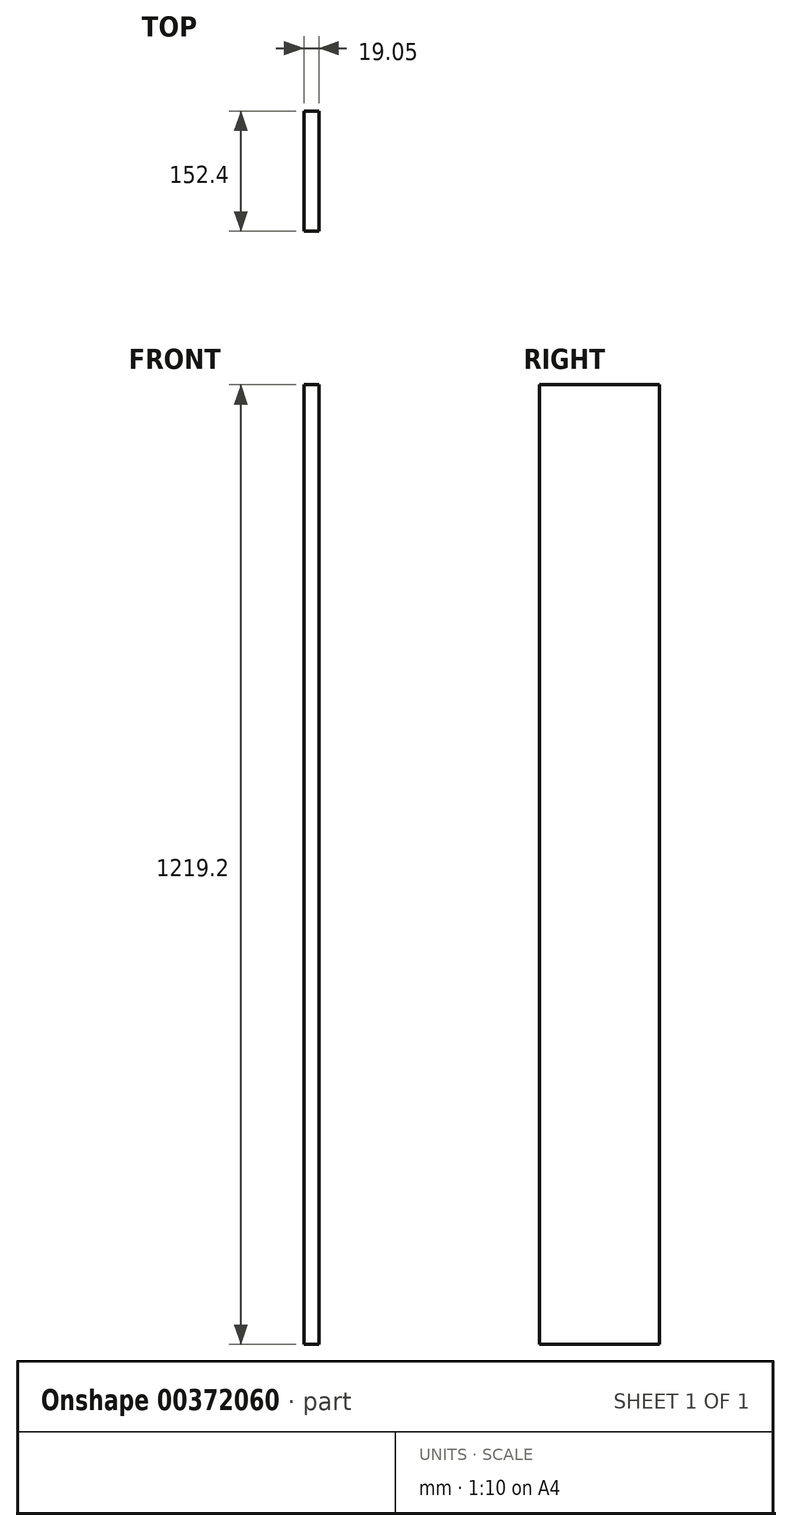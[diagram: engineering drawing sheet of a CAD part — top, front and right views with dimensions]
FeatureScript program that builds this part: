
annotation { "Feature Type Name" : "Feature", "Feature Type Description" : "" }
export const myFeature = defineFeature(function(context is Context, id is Id, definition is map)
    precondition{}
    {
        {
            var Q0;
            Q0=qCreatedBy(makeId("Right.planeOp"),FACE);
            var sketch = newSketch(context, id + "F0", { "sketchPlane" : qUnion([Q0])});
            skLineSegment(sketch, "E0.bottom", {"start": v(0, 0) * mm, "end": v(152.4, 0) * mm});
            skLineSegment(sketch, "E0.top", {"start": v(0, 1219.2) * mm, "end": v(152.4, 1219.2) * mm});
            skLineSegment(sketch, "E0.left", {"start": v(0, 0) * mm, "end": v(0, 1219.2) * mm});
            skLineSegment(sketch, "E0.right", {"start": v(152.4, 0) * mm, "end": v(152.4, 1219.2) * mm});
            skSolve(sketch);
        }
        {
            var Q0;
            Q0=makeQuery(id+"F0.imprint","IMPRINT",FACE,{"disambiguationData":[TD([[makeQuery(id+"F0.imprint","IMPRINT",EDGE,{"derivedFrom":sQuery(id+"F0.wireOp",EDGE,"E0.bottom")}),1.0]])]});
            extrude(context, id + "F1", {"entities" : qUnion([Q0]), "oppositeDirection" : true, "depth" : 19.05 * mm});
        }
    });
